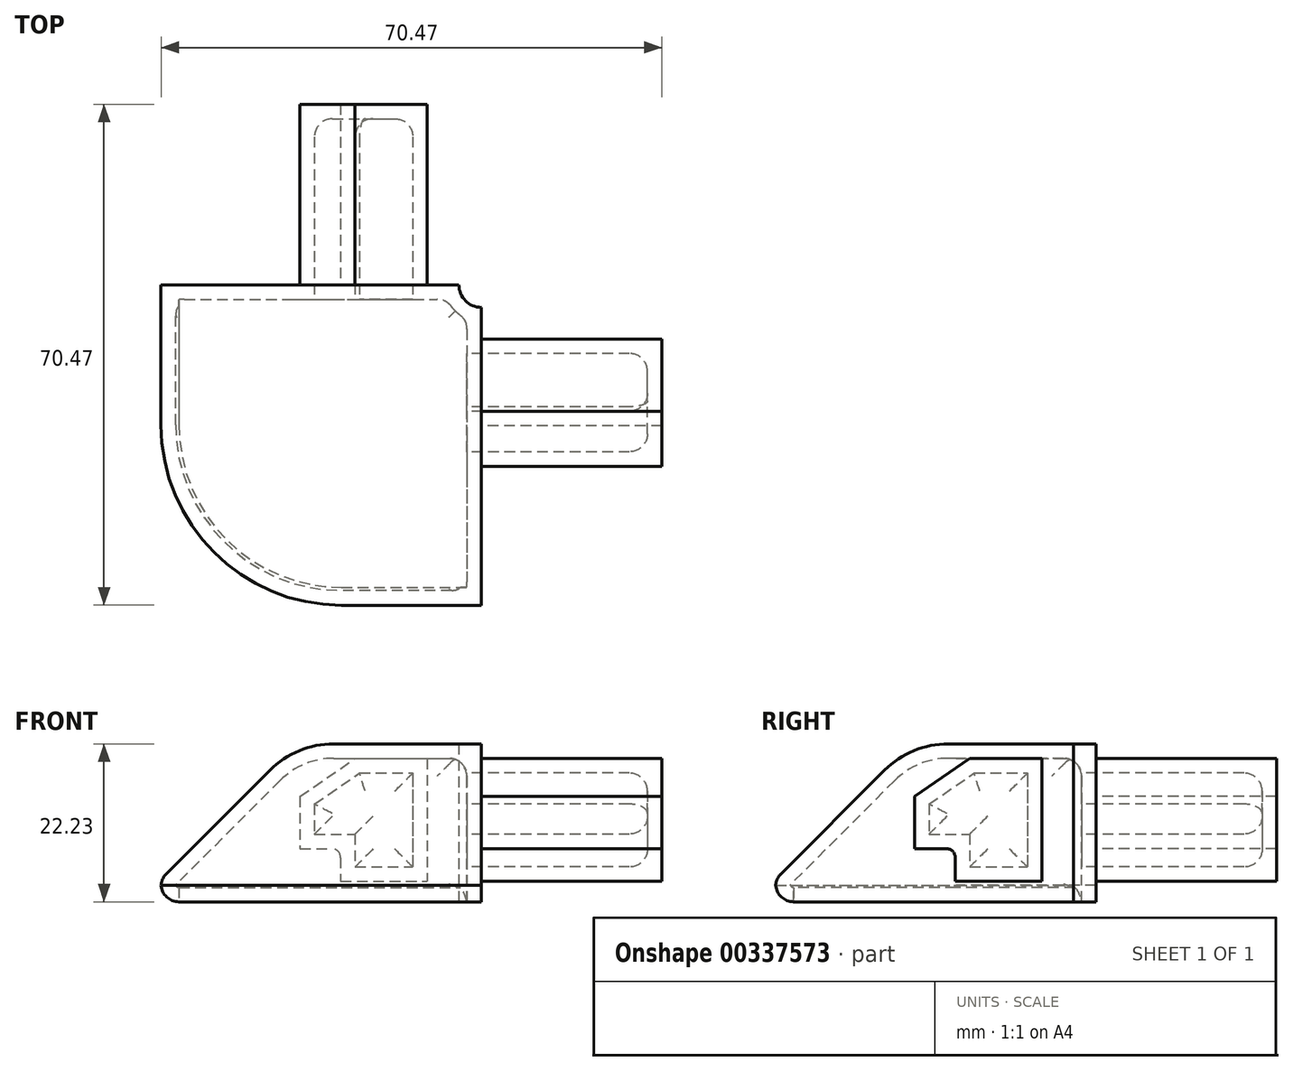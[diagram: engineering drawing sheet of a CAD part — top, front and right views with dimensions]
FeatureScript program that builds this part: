
annotation { "Feature Type Name" : "Feature", "Feature Type Description" : "" }
export const myFeature = defineFeature(function(context is Context, id is Id, definition is map)
    precondition{}
    {
        {
            var Q0;
            Q0=qCreatedBy(makeId("Top.planeOp"),FACE);
            var sketch = newSketch(context, id + "F0", { "sketchPlane" : qUnion([Q0])});
            skLineSegment(sketch, "E0.bottom", {"start": v(-22.54, 22.54) * mm, "end": v(19.37, 22.54) * mm});
            skLineSegment(sketch, "E0.top", {"start": v(2.86, -22.54) * mm, "end": v(22.54, -22.54) * mm});
            skLineSegment(sketch, "E0.left", {"start": v(-22.54, 22.54) * mm, "end": v(-22.54, 2.86) * mm});
            skLineSegment(sketch, "E0.right", {"start": v(22.54, 19.37) * mm, "end": v(22.54, -22.54) * mm});
            skPoint(sketch, "E1", {"position": v(0, 22.54) * mm});
            skPoint(sketch, "E2", {"position": v(22.54, 0) * mm});
            skPoint(sketch, "E3.visualSharp", {"position": v(-22.54, -22.54) * mm});
            skArc(sketch, "E3.filletArc", {"start": v(-22.54, 2.86) * mm, "mid": v(-15.1, -15.1) * mm, "end": v(2.86, -22.54) * mm});
            skArc(sketch, "E4", {"start": v(19.37, 22.54) * mm, "mid": v(20.3, 20.3) * mm, "end": v(22.54, 19.37) * mm});
            skSolve(sketch);
        }
        {
            var Q0;
            Q0 = qSketchRegion(id + "F0", true);
            extrude(context, id + "F1", {"entities" : qUnion([Q0]), "depth" : 22.22 * mm});
        }
        {
            var Q0;
            Q0=makeQuery(id+"F1.opExtrude","SWEPT_FACE",FACE,{"disambiguationData":[OSD([sQuery(id+"F0.wireOp",EDGE,"E0.right")])]});
            var sketch = newSketch(context, id + "F2", { "sketchPlane" : qUnion([Q0])});
            skLineSegment(sketch, "E5.0", {"start": v(22.54, 22.23) * mm, "end": v(22.54, 0) * mm, "construction": true});
            skLineSegment(sketch, "E6.0", {"start": v(19.37, 22.23) * mm, "end": v(-22.54, 22.23) * mm, "construction": true});
            skLineSegment(sketch, "E7.0", {"start": v(19.37, 0) * mm, "end": v(-22.54, 0) * mm, "construction": true});
            skLineSegment(sketch, "E8.bottom", {"start": v(4.76, 20.14) * mm, "end": v(14.92, 20.14) * mm});
            skLineSegment(sketch, "E8.top", {"start": v(2.73, 2.87) * mm, "end": v(14.92, 2.87) * mm});
            skLineSegment(sketch, "E8.left", {"start": v(-2.98, 14.8) * mm, "end": v(-2.98, 7.5) * mm});
            skLineSegment(sketch, "E8.right", {"start": v(14.92, 20.14) * mm, "end": v(14.92, 2.87) * mm});
            skPoint(sketch, "E9", {"position": v(4.76, 20.14) * mm});
            skPoint(sketch, "E10", {"position": v(-2.98, 14.8) * mm});
            skPoint(sketch, "E11", {"position": v(-2.98, 7.5) * mm});
            skPoint(sketch, "E12", {"position": v(2.73, 2.87) * mm});
            skLineSegment(sketch, "E13", {"start": v(-2.98, 14.8) * mm, "end": v(4.76, 20.14) * mm});
            skLineSegment(sketch, "E14", {"start": v(-2.98, 7.5) * mm, "end": v(2.73, 7.5) * mm});
            skLineSegment(sketch, "E15", {"start": v(2.73, 7.5) * mm, "end": v(2.73, 2.87) * mm});
            skPoint(sketch, "E16.orphan", {"position": v(-2.98, 2.87) * mm});
            skSolve(sketch);
        }
        {
            var Q0;
            Q0 = qSketchRegion(id + "F2", true);
            extrude(context, id + "F3", {"entities" : qUnion([Q0]), "operationType" : NewBodyOperationType.ADD, "depth" : 25.4 * mm});
        }
        {
            var Q0;
            Q0=makeQuery(id+"F1.opExtrude","SWEPT_FACE",FACE,{"disambiguationData":[OSD([sQuery(id+"F0.wireOp",EDGE,"E0.bottom")])]});
            var sketch = newSketch(context, id + "F4", { "sketchPlane" : qUnion([Q0])});
            skLineSegment(sketch, "E17.0", {"start": v(60.23, -8.26) * mm, "end": v(60.23, -30.48) * mm, "construction": true});
            skLineSegment(sketch, "E18.0", {"start": v(57.06, -8.26) * mm, "end": v(15.15, -8.26) * mm, "construction": true});
            skLineSegment(sketch, "E19.0", {"start": v(57.06, -30.48) * mm, "end": v(15.15, -30.48) * mm, "construction": true});
            skLineSegment(sketch, "E20.bottom", {"start": v(42.45, -10.34) * mm, "end": v(52.61, -10.34) * mm, "construction": true});
            skLineSegment(sketch, "E20.top", {"start": v(40.42, -27.61) * mm, "end": v(52.61, -27.61) * mm, "construction": true});
            skLineSegment(sketch, "E20.left", {"start": v(34.7, -15.67) * mm, "end": v(34.7, -22.99) * mm, "construction": true});
            skLineSegment(sketch, "E20.right", {"start": v(52.61, -10.34) * mm, "end": v(52.61, -27.61) * mm, "construction": true});
            skPoint(sketch, "E21", {"position": v(42.45, -10.34) * mm});
            skPoint(sketch, "E22", {"position": v(34.7, -15.67) * mm});
            skPoint(sketch, "E23", {"position": v(34.7, -22.99) * mm});
            skPoint(sketch, "E24", {"position": v(40.42, -27.61) * mm});
            skLineSegment(sketch, "E25", {"start": v(34.7, -15.67) * mm, "end": v(42.45, -10.34) * mm, "construction": true});
            skLineSegment(sketch, "E26", {"start": v(34.7, -22.99) * mm, "end": v(40.42, -22.99) * mm, "construction": true});
            skLineSegment(sketch, "E27", {"start": v(40.42, -22.99) * mm, "end": v(40.42, -27.61) * mm, "construction": true});
            skPoint(sketch, "E28.orphan", {"position": v(34.7, -27.61) * mm});
            skLineSegment(sketch, "E29.MirrorCS", {"start": v(2.98, 14.8) * mm, "end": v(-4.76, 20.14) * mm});
            skPoint(sketch, "E30.MirrorP", {"position": v(-2.73, 2.87) * mm});
            skLineSegment(sketch, "E31.MirrorCS", {"start": v(2.98, 7.5) * mm, "end": v(-2.73, 7.5) * mm});
            skLineSegment(sketch, "E32.MirrorCS", {"start": v(-2.73, 7.5) * mm, "end": v(-2.73, 2.87) * mm});
            skPoint(sketch, "E33.MirrorP", {"position": v(3.94, 3.05) * mm});
            skPoint(sketch, "E34.MirrorP", {"position": v(2.98, 7.5) * mm});
            skPoint(sketch, "E35.MirrorP", {"position": v(2.98, 14.8) * mm});
            skPoint(sketch, "E36.MirrorP", {"position": v(-4.76, 20.14) * mm});
            skLineSegment(sketch, "E37.MirrorCS", {"start": v(-4.76, 20.14) * mm, "end": v(-14.92, 20.14) * mm});
            skLineSegment(sketch, "E38.MirrorCS", {"start": v(-2.73, 2.87) * mm, "end": v(-14.92, 2.87) * mm});
            skLineSegment(sketch, "E39.MirrorCS", {"start": v(2.98, 14.8) * mm, "end": v(2.98, 7.5) * mm});
            skLineSegment(sketch, "E40.MirrorCS", {"start": v(-14.92, 20.14) * mm, "end": v(-14.92, 2.87) * mm});
            skLineSegment(sketch, "E41.0", {"start": v(-22.54, 22.23) * mm, "end": v(-22.54, 0) * mm, "construction": true});
            skLineSegment(sketch, "E42.0", {"start": v(22.54, 22.23) * mm, "end": v(-19.37, 22.23) * mm, "construction": true});
            skLineSegment(sketch, "E43.0", {"start": v(22.54, 0) * mm, "end": v(-19.37, 0) * mm, "construction": true});
            skLineSegment(sketch, "E44.0", {"start": v(-47.94, 20.14) * mm, "end": v(-22.54, 20.14) * mm, "construction": true});
            skSolve(sketch);
        }
        {
            var Q0;
            Q0=makeQuery(id+"F4.imprint","IMPRINT",FACE,{"disambiguationData":[TD([[makeQuery(id+"F4.imprint","IMPRINT",EDGE,{"derivedFrom":sQuery(id+"F4.wireOp",EDGE,"E29.MirrorCS")}),1.0]])]});
            extrude(context, id + "F5", {"entities" : qUnion([Q0]), "operationType" : NewBodyOperationType.ADD, "depth" : 25.4 * mm});
        }
        {
            var Q0;
            Q0=makeQuery(id+"F1.opExtrude","CAP_EDGE",EDGE,{"disambiguationData":[OSD([sQuery(id+"F0.wireOp",EDGE,"E3.filletArc")])],"isStart":false});
            chamfer(context, id + "F6", {"entities" : qUnion([Q0]), "width" : 19.05 * mm, "tangentPropagation" : true});
        }
        {
            var Q0;
            {var subQ0=sQuery(id+"F0.wireOp",EDGE,"E0.top");Q0=makeQuery(id+"F6.opChamfer","BLEND_EDGE",EDGE,{"blendedFrom":[makeQuery(id+"F1.opExtrude","CAP_EDGE",EDGE,{"disambiguationData":[OSD([subQ0])],"isStart":false}),makeQuery(id+"F1.opExtrude","CAP_FACE",FACE,{"disambiguationData":[OSD([sQuery(id+"F0.wireOp",EDGE,"E0.bottom"),subQ0,sQuery(id+"F0.wireOp",EDGE,"E0.left"),sQuery(id+"F0.wireOp",EDGE,"E0.right"),sQuery(id+"F0.wireOp",EDGE,"E3.filletArc"),sQuery(id+"F0.wireOp",EDGE,"E4")])],"isStart":false})],"blendedInto":[makeQuery(id+"F1.opExtrude","CAP_FACE",FACE,{"disambiguationData":[OSD([sQuery(id+"F0.wireOp",EDGE,"E0.bottom"),subQ0,sQuery(id+"F0.wireOp",EDGE,"E0.left"),sQuery(id+"F0.wireOp",EDGE,"E0.right"),sQuery(id+"F0.wireOp",EDGE,"E3.filletArc"),sQuery(id+"F0.wireOp",EDGE,"E4")])],"isStart":false})]});}
            fillet(context, id + "F7", {"entities" : qUnion([Q0]), "radius" : 12.7 * mm, "tangentPropagation" : true, "allowEdgeOverflow" : false});
        }
        {
            var Q0;
            {var subQ0=sQuery(id+"F0.wireOp",EDGE,"E0.left");Q0=makeQuery(id+"F6.opChamfer","BLEND_EDGE",EDGE,{"blendedFrom":[makeQuery(id+"F1.opExtrude","CAP_EDGE",EDGE,{"disambiguationData":[OSD([subQ0])],"isStart":false}),makeQuery(id+"F1.opExtrude","SWEPT_FACE",FACE,{"disambiguationData":[OSD([subQ0])]})],"blendedInto":[makeQuery(id+"F1.opExtrude","SWEPT_FACE",FACE,{"disambiguationData":[OSD([subQ0])]})]});}
            var Q1;
            Q1=makeQuery(id+"F1.opExtrude","CAP_EDGE",EDGE,{"disambiguationData":[OSD([sQuery(id+"F0.wireOp",EDGE,"E0.left")])],"isStart":true});
            fillet(context, id + "F8", {"entities" : qUnion([Q0, Q1]), "radius" : 2.54 * mm, "tangentPropagation" : true, "allowEdgeOverflow" : false});
        }
        {
            var Q0;
            Q0=makeQuery(id+"F1.opExtrude","CAP_FACE",FACE,{"disambiguationData":[OSD([sQuery(id+"F0.wireOp",EDGE,"E0.bottom"),sQuery(id+"F0.wireOp",EDGE,"E0.top"),sQuery(id+"F0.wireOp",EDGE,"E0.left"),sQuery(id+"F0.wireOp",EDGE,"E0.right"),sQuery(id+"F0.wireOp",EDGE,"E3.filletArc"),sQuery(id+"F0.wireOp",EDGE,"E4")])],"isStart":true});
            var Q1;
            Q1=makeQuery(id+"F1.opExtrude","SWEPT_BODY",BODY,{"disambiguationData":[OSD([sQuery(id+"F0.wireOp",EDGE,"E0.bottom"),sQuery(id+"F0.wireOp",EDGE,"E0.top"),sQuery(id+"F0.wireOp",EDGE,"E0.left"),sQuery(id+"F0.wireOp",EDGE,"E0.right"),sQuery(id+"F0.wireOp",EDGE,"E3.filletArc"),sQuery(id+"F0.wireOp",EDGE,"E4")])]});
            shell(context, id + "F9", {"entities" : qUnion([Q0]), "parts" : qUnion([Q1]), "thickness" : 2.03 * mm});
        }
        {
            var Q0;
            {var subQ0=sQuery(id+"F2.wireOp",EDGE,"E8.right");Q0=makeQuery(id+"F9.opShell","OFFSET_EDGE",EDGE,{"disambiguationData":[OSD([subQ0]),TDD([makeQuery(id+"F3.opExtrude","CAP_EDGE",EDGE,{"disambiguationData":[OSD([subQ0])],"isStart":true})])]});}
            var Q1;
            {var subQ0=sQuery(id+"F2.wireOp",EDGE,"E8.bottom");Q1=makeQuery(id+"F9.opShell","OFFSET_EDGE",EDGE,{"disambiguationData":[OSD([subQ0]),TDD([makeQuery(id+"F3.opExtrude","CAP_EDGE",EDGE,{"disambiguationData":[OSD([subQ0])],"isStart":true})])]});}
            var Q2;
            {var subQ0=sQuery(id+"F2.wireOp",EDGE,"E13");Q2=makeQuery(id+"F9.opShell","OFFSET_EDGE",EDGE,{"disambiguationData":[OSD([subQ0]),TDD([makeQuery(id+"F3.opExtrude","CAP_EDGE",EDGE,{"disambiguationData":[OSD([subQ0])],"isStart":true})])]});}
            var Q3;
            {var subQ0=sQuery(id+"F2.wireOp",EDGE,"E8.left");Q3=makeQuery(id+"F9.opShell","OFFSET_EDGE",EDGE,{"disambiguationData":[OSD([subQ0]),TDD([makeQuery(id+"F3.opExtrude","CAP_EDGE",EDGE,{"disambiguationData":[OSD([subQ0])],"isStart":true})])]});}
            var Q4;
            {var subQ0=sQuery(id+"F2.wireOp",EDGE,"E14");Q4=makeQuery(id+"F9.opShell","OFFSET_EDGE",EDGE,{"disambiguationData":[OSD([subQ0]),TDD([makeQuery(id+"F3.opExtrude","CAP_EDGE",EDGE,{"disambiguationData":[OSD([subQ0])],"isStart":true})])]});}
            var Q5;
            {var subQ0=sQuery(id+"F2.wireOp",EDGE,"E15");Q5=makeQuery(id+"F9.opShell","OFFSET_EDGE",EDGE,{"disambiguationData":[OSD([subQ0]),TDD([makeQuery(id+"F3.opExtrude","CAP_EDGE",EDGE,{"disambiguationData":[OSD([subQ0])],"isStart":true})])]});}
            var Q6;
            {var subQ0=sQuery(id+"F2.wireOp",EDGE,"E8.top");Q6=makeQuery(id+"F9.opShell","OFFSET_EDGE",EDGE,{"disambiguationData":[OSD([subQ0]),TDD([makeQuery(id+"F3.opExtrude","CAP_EDGE",EDGE,{"disambiguationData":[OSD([subQ0])],"isStart":true})])]});}
            var Q7;
            {var subQ0=sQuery(id+"F4.wireOp",EDGE,"E37.MirrorCS");Q7=makeQuery(id+"F9.opShell","OFFSET_EDGE",EDGE,{"disambiguationData":[OSD([subQ0]),TDD([makeQuery(id+"F5.opExtrude","CAP_EDGE",EDGE,{"disambiguationData":[OSD([subQ0])],"isStart":true})])]});}
            var Q8;
            {var subQ0=sQuery(id+"F4.wireOp",EDGE,"E40.MirrorCS");Q8=makeQuery(id+"F9.opShell","OFFSET_EDGE",EDGE,{"disambiguationData":[OSD([subQ0]),TDD([makeQuery(id+"F5.opExtrude","CAP_EDGE",EDGE,{"disambiguationData":[OSD([subQ0])],"isStart":true})])]});}
            var Q9;
            {var subQ0=sQuery(id+"F4.wireOp",EDGE,"E38.MirrorCS");Q9=makeQuery(id+"F9.opShell","OFFSET_EDGE",EDGE,{"disambiguationData":[OSD([subQ0]),TDD([makeQuery(id+"F5.opExtrude","CAP_EDGE",EDGE,{"disambiguationData":[OSD([subQ0])],"isStart":true})])]});}
            var Q10;
            {var subQ0=sQuery(id+"F4.wireOp",EDGE,"E32.MirrorCS");Q10=makeQuery(id+"F9.opShell","OFFSET_EDGE",EDGE,{"disambiguationData":[OSD([subQ0]),TDD([makeQuery(id+"F5.opExtrude","CAP_EDGE",EDGE,{"disambiguationData":[OSD([subQ0])],"isStart":true})])]});}
            var Q11;
            {var subQ0=sQuery(id+"F4.wireOp",EDGE,"E31.MirrorCS");Q11=makeQuery(id+"F9.opShell","OFFSET_EDGE",EDGE,{"disambiguationData":[OSD([subQ0]),TDD([makeQuery(id+"F5.opExtrude","CAP_EDGE",EDGE,{"disambiguationData":[OSD([subQ0])],"isStart":true})])]});}
            var Q12;
            {var subQ0=sQuery(id+"F4.wireOp",EDGE,"E39.MirrorCS");Q12=makeQuery(id+"F9.opShell","OFFSET_EDGE",EDGE,{"disambiguationData":[OSD([subQ0]),TDD([makeQuery(id+"F5.opExtrude","CAP_EDGE",EDGE,{"disambiguationData":[OSD([subQ0])],"isStart":true})])]});}
            var Q13;
            {var subQ0=sQuery(id+"F4.wireOp",EDGE,"E29.MirrorCS");Q13=makeQuery(id+"F9.opShell","OFFSET_EDGE",EDGE,{"disambiguationData":[OSD([subQ0]),TDD([makeQuery(id+"F5.opExtrude","CAP_EDGE",EDGE,{"disambiguationData":[OSD([subQ0])],"isStart":true})])]});}
            fillet(context, id + "F10", {"entities" : qUnion([Q0, Q1, Q2, Q3, Q4, Q5, Q6, Q7, Q8, Q9, Q10, Q11, Q12, Q13]), "radius" : 2.54 * mm, "tangentPropagation" : true, "allowEdgeOverflow" : false});
        }
        {
            var Q0;
            Q0=makeQuery(id+"F5.opExtrude","SWEPT_EDGE",EDGE,{"disambiguationData":[OSD([sQuery(id+"F4.wireOp",EDGE,"E31.MirrorCS"),sQuery(id+"F4.wireOp",EDGE,"E32.MirrorCS")])]});
            var Q1;
            Q1=makeQuery(id+"F3.opExtrude","SWEPT_EDGE",EDGE,{"disambiguationData":[OSD([sQuery(id+"F2.wireOp",EDGE,"E14"),sQuery(id+"F2.wireOp",EDGE,"E15")])]});
            fillet(context, id + "F11", {"entities" : qUnion([Q0, Q1]), "radius" : 1.27 * mm, "tangentPropagation" : true, "allowEdgeOverflow" : false});
        }
        {
            var Q0;
            Q0=makeQuery(id+"F9.opShell","OFFSET_EDGE",EDGE,{"disambiguationData":[OSD([sQuery(id+"F0.wireOp",EDGE,"E0.bottom"),sQuery(id+"F0.wireOp",EDGE,"E4")])]});
            var Q1;
            Q1=makeQuery(id+"F9.opShell","OFFSET_EDGE",EDGE,{"disambiguationData":[OSD([sQuery(id+"F0.wireOp",EDGE,"E0.right"),sQuery(id+"F0.wireOp",EDGE,"E4")])]});
            var Q2;
            {var subQ0=sQuery(id+"F0.wireOp",EDGE,"E0.bottom");var subQ1=sQuery(id+"F0.wireOp",EDGE,"E4");var subQ2=sQuery(id+"F0.wireOp",EDGE,"E3.filletArc");var subQ3=sQuery(id+"F0.wireOp",EDGE,"E0.right");var subQ4=sQuery(id+"F0.wireOp",EDGE,"E0.left");var subQ5=sQuery(id+"F0.wireOp",EDGE,"E0.top");Q2=makeQuery(id+"F9.opShell","OFFSET_EDGE",EDGE,{"disambiguationData":[OSD([subQ0,subQ5,subQ4,subQ3,subQ2,subQ1]),TDD([makeQuery(id+"F7.opFillet","BLEND_EDGE",EDGE,{"blendedFrom":[makeQuery(id+"F6.opChamfer","BLEND_EDGE",EDGE,{"blendedFrom":[makeQuery(id+"F1.opExtrude","CAP_EDGE",EDGE,{"disambiguationData":[OSD([subQ4])],"isStart":false}),makeQuery(id+"F1.opExtrude","CAP_FACE",FACE,{"disambiguationData":[OSD([subQ0,subQ5,subQ4,subQ3,subQ2,subQ1])],"isStart":false})],"blendedInto":[makeQuery(id+"F1.opExtrude","CAP_FACE",FACE,{"disambiguationData":[OSD([subQ0,subQ5,subQ4,subQ3,subQ2,subQ1])],"isStart":false})]}),makeQuery(id+"F1.opExtrude","SWEPT_FACE",FACE,{"disambiguationData":[OSD([subQ0])]})],"blendedInto":[makeQuery(id+"F1.opExtrude","SWEPT_FACE",FACE,{"disambiguationData":[OSD([subQ0])]})]})])]});}
            var Q3;
            {var subQ0=sQuery(id+"F0.wireOp",EDGE,"E0.right");var subQ1=sQuery(id+"F0.wireOp",EDGE,"E0.top");Q3=makeQuery(id+"F9.opShell","OFFSET_EDGE",EDGE,{"disambiguationData":[OSD([subQ1,subQ0]),TDD([makeQuery(id+"F6.opChamfer","BLEND_EDGE",EDGE,{"blendedFrom":[makeQuery(id+"F1.opExtrude","CAP_EDGE",EDGE,{"disambiguationData":[OSD([subQ1])],"isStart":false}),makeQuery(id+"F1.opExtrude","SWEPT_FACE",FACE,{"disambiguationData":[OSD([subQ0])]})],"blendedInto":[makeQuery(id+"F1.opExtrude","SWEPT_FACE",FACE,{"disambiguationData":[OSD([subQ0])]})]})])]});}
            fillet(context, id + "F12", {"entities" : qUnion([Q0, Q1, Q2, Q3]), "radius" : 2.54 * mm, "tangentPropagation" : true, "allowEdgeOverflow" : false});
        }
    });
